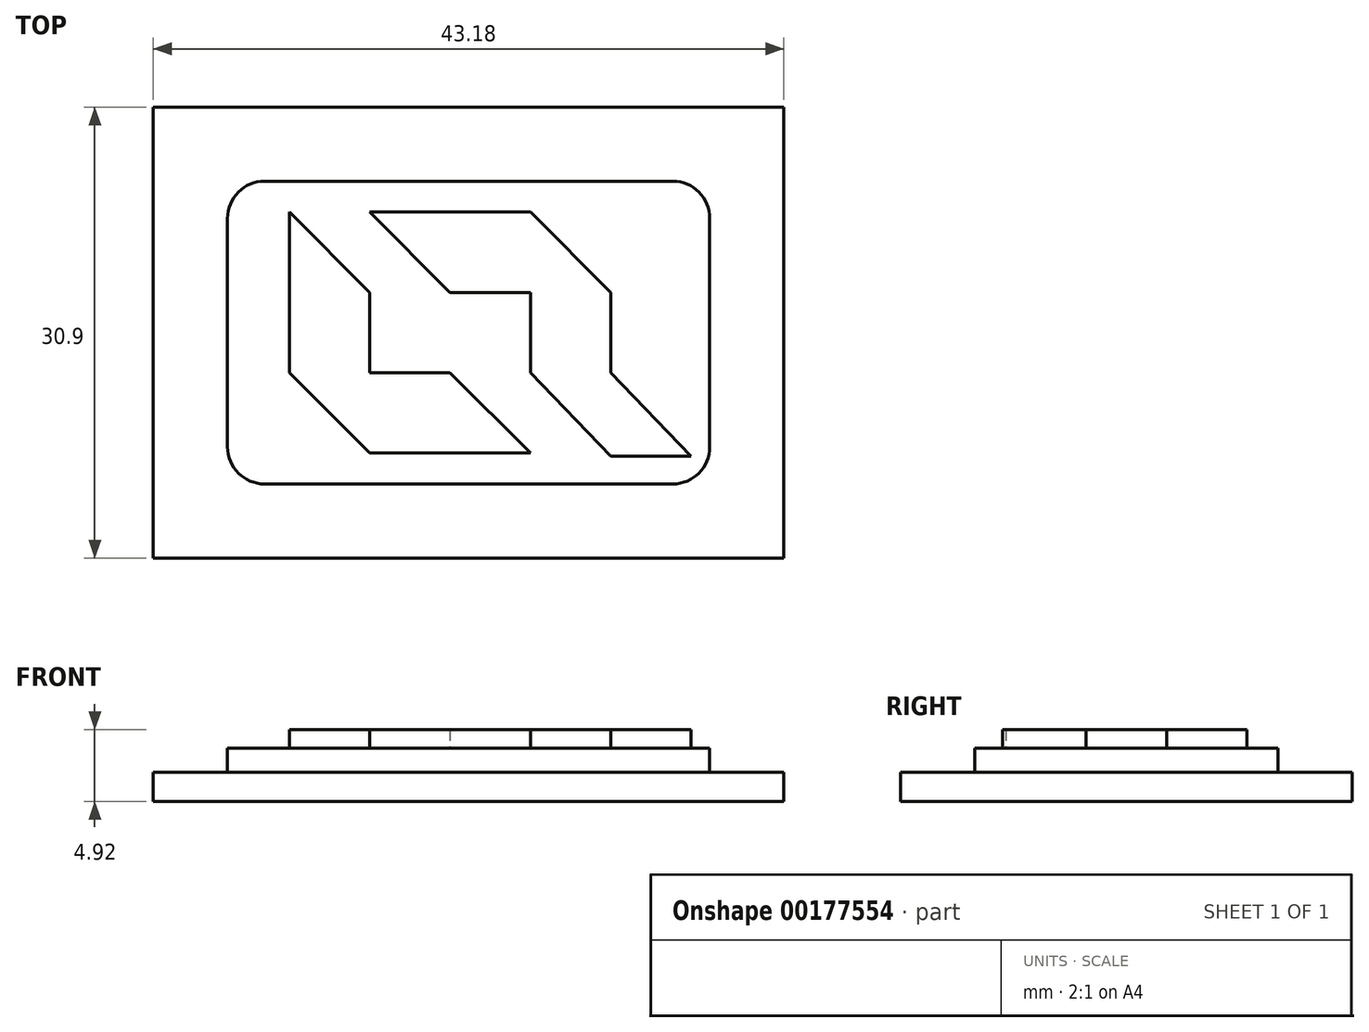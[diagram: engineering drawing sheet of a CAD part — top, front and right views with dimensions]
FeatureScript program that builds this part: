
annotation { "Feature Type Name" : "Feature", "Feature Type Description" : "" }
export const myFeature = defineFeature(function(context is Context, id is Id, definition is map)
    precondition{}
    {
        {
            var Q0;
            Q0=qCreatedBy(makeId("Top.planeOp"),FACE);
            var sketch = newSketch(context, id + "F0", { "sketchPlane" : qUnion([Q0])});
            skLineSegment(sketch, "E0.bottom", {"start": v(25.4, 38.1) * mm, "end": v(-25.4, 38.1) * mm});
            skLineSegment(sketch, "E0.top", {"start": v(25.4, -38.1) * mm, "end": v(-25.4, -38.1) * mm});
            skLineSegment(sketch, "E0.left", {"start": v(25.4, 38.1) * mm, "end": v(25.4, -38.1) * mm});
            skLineSegment(sketch, "E0.right", {"start": v(-25.4, 38.1) * mm, "end": v(-25.4, -38.1) * mm});
            skPoint(sketch, "E0.middle", {"position": v(0, 0) * mm});
            skLineSegment(sketch, "E1", {"start": v(-11, 29.97) * mm, "end": v(-11, 24.47) * mm});
            skLineSegment(sketch, "E2", {"start": v(-11, 24.47) * mm, "end": v(-5.5, 24.47) * mm});
            skLineSegment(sketch, "E3", {"start": v(-5.5, 24.47) * mm, "end": v(-11, 29.97) * mm});
            skLineSegment(sketch, "E4", {"start": v(-11, 24.47) * mm, "end": v(-11, 18.97) * mm});
            skLineSegment(sketch, "E5", {"start": v(-11, 18.97) * mm, "end": v(-5.5, 13.47) * mm});
            skLineSegment(sketch, "E6", {"start": v(0, 18.97) * mm, "end": v(5.5, 13.47) * mm});
            skLineSegment(sketch, "E7", {"start": v(-5.5, 24.47) * mm, "end": v(-5.5, 18.97) * mm});
            skLineSegment(sketch, "E8", {"start": v(-11, 18.97) * mm, "end": v(-5.5, 18.97) * mm});
            skLineSegment(sketch, "E9", {"start": v(-5.5, 18.97) * mm, "end": v(0, 18.97) * mm});
            skLineSegment(sketch, "E10", {"start": v(-5.5, 13.47) * mm, "end": v(0, 13.47) * mm});
            skLineSegment(sketch, "E11", {"start": v(0, 13.47) * mm, "end": v(5.5, 13.47) * mm});
            skLineSegment(sketch, "E12", {"start": v(-11, 24.47) * mm, "end": v(-5.5, 18.97) * mm});
            skLineSegment(sketch, "E13", {"start": v(-5.5, 18.97) * mm, "end": v(-5.5, 13.47) * mm});
            skLineSegment(sketch, "E14", {"start": v(-5.5, 29.97) * mm, "end": v(5.5, 29.97) * mm});
            skLineSegment(sketch, "E15", {"start": v(5.5, 29.97) * mm, "end": v(11, 24.47) * mm});
            skLineSegment(sketch, "E16", {"start": v(11, 24.47) * mm, "end": v(5.5, 24.47) * mm});
            skLineSegment(sketch, "E17", {"start": v(5.5, 24.47) * mm, "end": v(0, 24.47) * mm});
            skLineSegment(sketch, "E18", {"start": v(0, 24.47) * mm, "end": v(-5.5, 29.97) * mm});
            skLineSegment(sketch, "E19", {"start": v(5.5, 24.47) * mm, "end": v(5.5, 18.97) * mm});
            skLineSegment(sketch, "E20", {"start": v(5.5, 18.97) * mm, "end": v(11, 13.25) * mm});
            skLineSegment(sketch, "E21", {"start": v(11, 13.25) * mm, "end": v(16.5, 13.25) * mm});
            skLineSegment(sketch, "E22", {"start": v(16.5, 13.25) * mm, "end": v(11, 18.97) * mm});
            skLineSegment(sketch, "E23", {"start": v(11, 18.97) * mm, "end": v(11, 24.47) * mm});
            skLineSegment(sketch, "E24", {"start": v(0, 24.47) * mm, "end": v(0, 29.97) * mm});
            skLineSegment(sketch, "E25", {"start": v(5.5, 29.97) * mm, "end": v(5.5, 24.47) * mm});
            skText(sketch, "E26", { "text": "IN", "fontName": "RobotoSlab-Regular.ttf"});
            skText(sketch, "E27", { "text": "ROBOT", "fontName": "RobotoSlab-Regular.ttf"});
            skText(sketch, "E28", { "text": "WE TRUST", "fontName": "RobotoSlab-Regular.ttf"});
            skLineSegment(sketch, "E29.bottom", {"start": v(-5.5, -7.16) * mm, "end": v(-20.73, -7.16) * mm});
            skLineSegment(sketch, "E29.top", {"start": v(-5.5, -7.92) * mm, "end": v(-20.73, -7.92) * mm});
            skLineSegment(sketch, "E29.left", {"start": v(-5.5, -7.16) * mm, "end": v(-5.5, -7.92) * mm});
            skLineSegment(sketch, "E29.right", {"start": v(-20.73, -7.16) * mm, "end": v(-20.73, -7.92) * mm});
            skLineSegment(sketch, "E30.bottom", {"start": v(-5.5, -8.68) * mm, "end": v(-15.65, -8.68) * mm});
            skLineSegment(sketch, "E30.top", {"start": v(-5.5, -9.45) * mm, "end": v(-15.65, -9.45) * mm});
            skLineSegment(sketch, "E30.left", {"start": v(-5.5, -8.68) * mm, "end": v(-5.5, -9.45) * mm});
            skLineSegment(sketch, "E30.right", {"start": v(-15.65, -8.68) * mm, "end": v(-15.65, -9.45) * mm});
            skLineSegment(sketch, "E31.bottom", {"start": v(-5.5, -10.2) * mm, "end": v(-10.57, -10.2) * mm});
            skLineSegment(sketch, "E31.top", {"start": v(-5.5, -10.97) * mm, "end": v(-10.57, -10.97) * mm});
            skLineSegment(sketch, "E31.left", {"start": v(-5.5, -10.2) * mm, "end": v(-5.5, -10.97) * mm});
            skLineSegment(sketch, "E31.right", {"start": v(-10.57, -10.2) * mm, "end": v(-10.57, -10.97) * mm});
            skLineSegment(sketch, "E32.MirrorCS", {"start": v(20.73, -7.16) * mm, "end": v(20.73, -7.92) * mm});
            skLineSegment(sketch, "E33.MirrorCS", {"start": v(5.5, -7.16) * mm, "end": v(5.5, -7.92) * mm});
            skLineSegment(sketch, "E34.MirrorCS", {"start": v(5.5, -8.68) * mm, "end": v(15.65, -8.68) * mm});
            skLineSegment(sketch, "E35.MirrorCS", {"start": v(5.5, -8.68) * mm, "end": v(5.5, -9.45) * mm});
            skLineSegment(sketch, "E36.MirrorCS", {"start": v(15.65, -8.68) * mm, "end": v(15.65, -9.45) * mm});
            skLineSegment(sketch, "E37.MirrorCS", {"start": v(5.5, -9.45) * mm, "end": v(15.65, -9.45) * mm});
            skLineSegment(sketch, "E38.MirrorCS", {"start": v(5.5, -10.2) * mm, "end": v(10.57, -10.2) * mm});
            skLineSegment(sketch, "E39.MirrorCS", {"start": v(10.57, -10.2) * mm, "end": v(10.57, -10.97) * mm});
            skLineSegment(sketch, "E40.MirrorCS", {"start": v(5.5, -10.2) * mm, "end": v(5.5, -10.97) * mm});
            skLineSegment(sketch, "E41.MirrorCS", {"start": v(5.5, -10.97) * mm, "end": v(10.57, -10.97) * mm});
            skLineSegment(sketch, "E42.MirrorCS", {"start": v(5.5, -7.16) * mm, "end": v(20.73, -7.16) * mm});
            skLineSegment(sketch, "E43.MirrorCS", {"start": v(5.5, -7.92) * mm, "end": v(20.73, -7.92) * mm});
            skLineSegment(sketch, "E44", {"start": v(-4.14, -29.96) * mm, "end": v(-4.14, -31.27) * mm, "construction": true});
            skLineSegment(sketch, "E45", {"start": v(-4.14, -31.27) * mm, "end": v(-0.86, -31.27) * mm, "construction": true});
            skLineSegment(sketch, "E46", {"start": v(-0.86, -31.27) * mm, "end": v(-0.86, -27.79) * mm, "construction": true});
            skLineSegment(sketch, "E47", {"start": v(-0.86, -27.79) * mm, "end": v(-10.42, -27.79) * mm, "construction": true});
            skLineSegment(sketch, "E48", {"start": v(-10.42, -27.79) * mm, "end": v(-10.42, -32.56) * mm, "construction": true});
            skArc(sketch, "E49", {"start": v(-4.14, -29.96) * mm, "mid": v(-4.8, -30.62) * mm, "end": v(-4.14, -31.27) * mm});
            skArc(sketch, "E50", {"start": v(-4.14, -31.27) * mm, "mid": v(-2.4, -29.53) * mm, "end": v(-4.14, -27.79) * mm});
            skArc(sketch, "E51", {"start": v(-4.14, -27.79) * mm, "mid": v(-8.08, -29.11) * mm, "end": v(-10.42, -32.56) * mm});
            skLineSegment(sketch, "E52", {"start": v(-10.42, -32.56) * mm, "end": v(-10.21, -32.56) * mm});
            skArc(sketch, "E53", {"start": v(-4.14, -28.04) * mm, "mid": v(-7.9, -29.33) * mm, "end": v(-10.21, -32.56) * mm});
            const initialGuessF0  = {"E26": [-0.00295, -0.01097, 1, 0, 0.00381], "E27": [-0.00904, -0.01732, 1, 0, 0.00381], "E28": [-0.01364, -0.02367, 1, 0, 0.0038]};
            skSetInitialGuess(sketch, initialGuessF0);
            skSolve(sketch);
        }
        {
            var Q0;
            Q0=makeQuery(id+"F0.imprint","IMPRINT",FACE,{"disambiguationData":[TD([[makeQuery(id+"F0.imprint","IMPRINT",EDGE,{"derivedFrom":sQuery(id+"F0.wireOp",EDGE,"E0.bottom")}),1.0]])]});
            var sketch = newSketch(context, id + "F1", { "sketchPlane" : qUnion([Q0])});
            skLineSegment(sketch, "E54", {"start": v(-11, 29.97) * mm, "end": v(-11, 18.97) * mm});
            skLineSegment(sketch, "E55", {"start": v(-11, 18.97) * mm, "end": v(-5.5, 13.47) * mm});
            skLineSegment(sketch, "E56", {"start": v(-5.5, 13.47) * mm, "end": v(5.5, 13.47) * mm});
            skLineSegment(sketch, "E57", {"start": v(5.5, 13.47) * mm, "end": v(0, 18.97) * mm});
            skLineSegment(sketch, "E58", {"start": v(0, 18.97) * mm, "end": v(-5.5, 18.97) * mm});
            skLineSegment(sketch, "E59", {"start": v(-5.5, 18.97) * mm, "end": v(-5.5, 24.47) * mm});
            skLineSegment(sketch, "E60", {"start": v(-5.5, 24.47) * mm, "end": v(-11, 29.97) * mm});
            skLineSegment(sketch, "E61", {"start": v(-5.5, 29.97) * mm, "end": v(5.5, 29.97) * mm});
            skLineSegment(sketch, "E62", {"start": v(5.5, 29.97) * mm, "end": v(11, 24.47) * mm});
            skLineSegment(sketch, "E63", {"start": v(11, 24.47) * mm, "end": v(11, 18.97) * mm});
            skLineSegment(sketch, "E64", {"start": v(11, 18.97) * mm, "end": v(16.5, 13.25) * mm});
            skLineSegment(sketch, "E65", {"start": v(16.5, 13.25) * mm, "end": v(11, 13.25) * mm});
            skLineSegment(sketch, "E66", {"start": v(11, 13.25) * mm, "end": v(5.5, 18.97) * mm});
            skLineSegment(sketch, "E67", {"start": v(5.5, 18.97) * mm, "end": v(5.5, 24.47) * mm});
            skLineSegment(sketch, "E68", {"start": v(5.5, 24.47) * mm, "end": v(0, 24.47) * mm});
            skLineSegment(sketch, "E69", {"start": v(0, 24.47) * mm, "end": v(-5.5, 29.97) * mm});
            skSolve(sketch);
        }
        {
            var Q0;
            Q0=makeQuery(id+"F0.imprint","IMPRINT",FACE,{"disambiguationData":[TD([[makeQuery(id+"F0.imprint","IMPRINT",EDGE,{"derivedFrom":sQuery(id+"F0.wireOp",EDGE,"E0.bottom")}),1.0]])]});
            var sketch = newSketch(context, id + "F2", { "sketchPlane" : qUnion([Q0])});
            skLineSegment(sketch, "E70.bottom", {"start": v(-12.7, 32.1) * mm, "end": v(15.24, 32.1) * mm});
            skLineSegment(sketch, "E70.top", {"start": v(-12.7, 11.35) * mm, "end": v(15.24, 11.35) * mm});
            skLineSegment(sketch, "E70.left", {"start": v(-15.24, 29.55) * mm, "end": v(-15.24, 13.89) * mm});
            skLineSegment(sketch, "E70.right", {"start": v(17.78, 29.55) * mm, "end": v(17.78, 13.89) * mm});
            skPoint(sketch, "E71.visualSharp", {"position": v(-15.24, 32.1) * mm});
            skArc(sketch, "E71.filletArc", {"start": v(-12.7, 32.1) * mm, "mid": v(-14.5, 31.35) * mm, "end": v(-15.24, 29.55) * mm});
            skPoint(sketch, "E72.visualSharp", {"position": v(17.78, 32.1) * mm});
            skArc(sketch, "E72.filletArc", {"start": v(17.78, 29.55) * mm, "mid": v(17.04, 31.35) * mm, "end": v(15.24, 32.1) * mm});
            skPoint(sketch, "E73.visualSharp", {"position": v(17.78, 11.35) * mm});
            skArc(sketch, "E73.filletArc", {"start": v(15.24, 11.35) * mm, "mid": v(17.04, 12.1) * mm, "end": v(17.78, 13.89) * mm});
            skPoint(sketch, "E74.visualSharp", {"position": v(-15.24, 11.35) * mm});
            skArc(sketch, "E74.filletArc", {"start": v(-15.24, 13.89) * mm, "mid": v(-14.5, 12.1) * mm, "end": v(-12.7, 11.35) * mm});
            skSolve(sketch);
        }
        {
            var Q0;
            Q0 = qSketchRegion(id + "F2", true);
            extrude(context, id + "F3", {"entities" : qUnion([Q0]), "oppositeDirection" : true, "depth" : 1.65 * mm});
        }
        {
            var Q0;
            Q0 = qSketchRegion(id + "F1", true);
            extrude(context, id + "F4", {"entities" : qUnion([Q0]), "operationType" : NewBodyOperationType.ADD, "depth" : 1.27 * mm});
        }
        {
            var Q0;
            Q0=makeQuery(id+"F3.opExtrude","CAP_FACE",FACE,{"disambiguationData":[OSD([sQuery(id+"F2.wireOp",EDGE,"E70.bottom"),sQuery(id+"F2.wireOp",EDGE,"E70.top"),sQuery(id+"F2.wireOp",EDGE,"E70.left"),sQuery(id+"F2.wireOp",EDGE,"E70.right"),sQuery(id+"F2.wireOp",EDGE,"E71.filletArc"),sQuery(id+"F2.wireOp",EDGE,"E72.filletArc"),sQuery(id+"F2.wireOp",EDGE,"E73.filletArc"),sQuery(id+"F2.wireOp",EDGE,"E74.filletArc")])],"isStart":false});
            var sketch = newSketch(context, id + "F5", { "sketchPlane" : qUnion([Q0])});
            skLineSegment(sketch, "E75.bottom", {"start": v(-20.32, -37.17) * mm, "end": v(22.86, -37.17) * mm});
            skLineSegment(sketch, "E75.top", {"start": v(-20.32, -6.27) * mm, "end": v(22.86, -6.27) * mm});
            skLineSegment(sketch, "E75.left", {"start": v(-20.32, -37.17) * mm, "end": v(-20.32, -6.27) * mm});
            skLineSegment(sketch, "E75.right", {"start": v(22.86, -37.17) * mm, "end": v(22.86, -6.27) * mm});
            skSolve(sketch);
        }
        {
            var Q0;
            Q0 = qSketchRegion(id + "F5", true);
            extrude(context, id + "F6", {"entities" : qUnion([Q0]), "operationType" : NewBodyOperationType.ADD, "depth" : 2 * mm});
        }
    });
